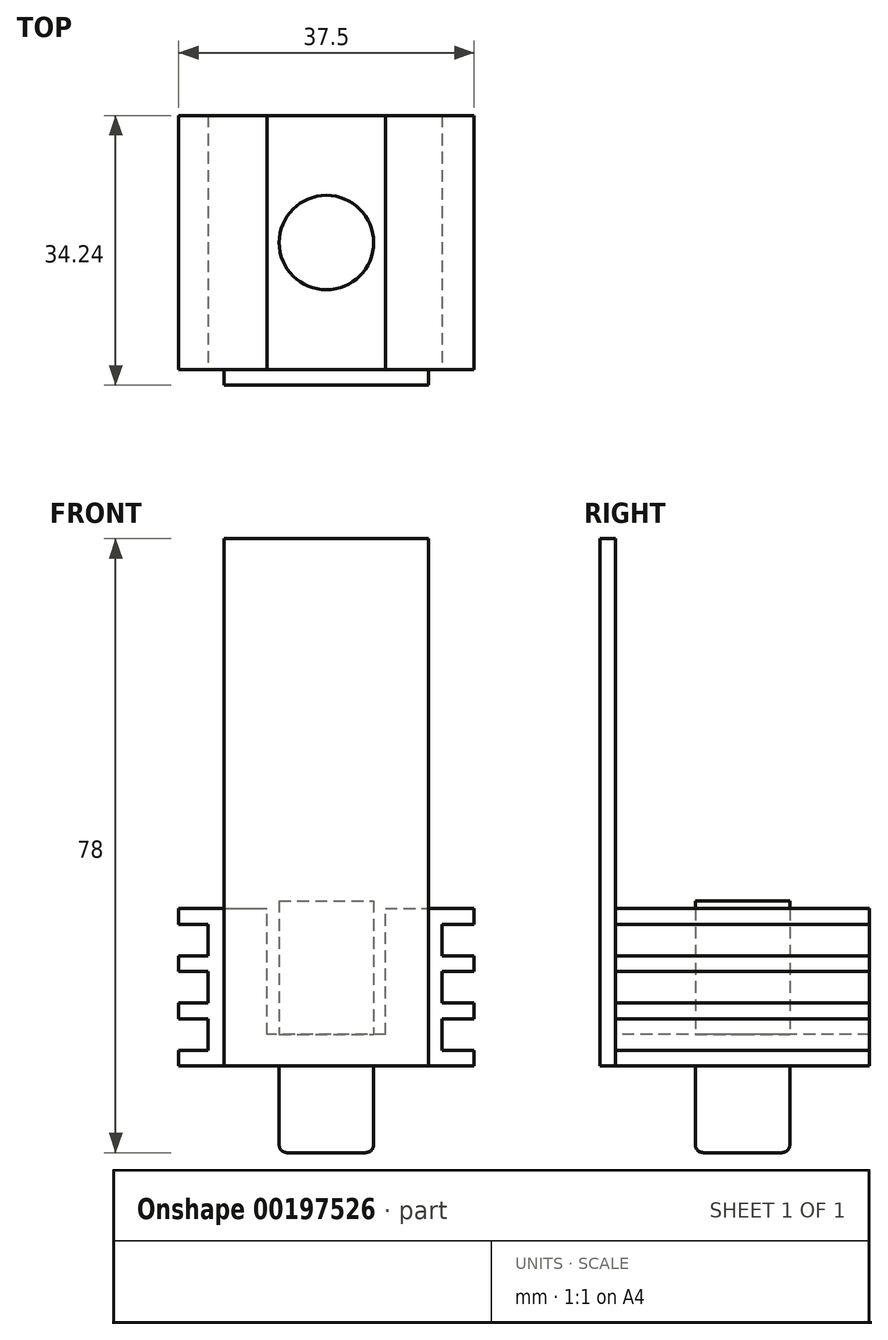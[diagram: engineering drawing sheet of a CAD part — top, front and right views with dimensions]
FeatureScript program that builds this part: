
annotation { "Feature Type Name" : "Feature", "Feature Type Description" : "" }
export const myFeature = defineFeature(function(context is Context, id is Id, definition is map)
    precondition{}
    {
        {
            var Q0;
            Q0=qCreatedBy(makeId("Top.planeOp"),FACE);
            var sketch = newSketch(context, id + "F0", { "sketchPlane" : qUnion([Q0])});
            skLineSegment(sketch, "E0.bottom", {"start": v(-18.75, 16.12) * mm, "end": v(18.75, 16.13) * mm});
            skLineSegment(sketch, "E0.top", {"start": v(-18.75, -16.13) * mm, "end": v(18.75, -16.13) * mm});
            skLineSegment(sketch, "E0.left", {"start": v(-18.75, 16.12) * mm, "end": v(-18.75, -16.13) * mm});
            skLineSegment(sketch, "E0.right", {"start": v(18.75, 16.13) * mm, "end": v(18.75, -16.12) * mm});
            skCircle(sketch, "E1", {"center": v(0, 0) * mm, "radius": 6 * mm, "construction": true});
            skSolve(sketch);
        }
        {
            var Q0;
            Q0=qSketchRegion(id+"F0",true);
            extrude(context, id + "F1", {"entities" : qUnion([Q0]), "depth" : 20 * mm});
        }
        {
            var Q0;
            Q0=makeQuery(id+"F1.opExtrude","CAP_FACE",FACE,{"disambiguationData":[OSD([sQuery(id+"F0.wireOp",EDGE,"E0.bottom"),sQuery(id+"F0.wireOp",EDGE,"E0.top"),sQuery(id+"F0.wireOp",EDGE,"E0.left"),sQuery(id+"F0.wireOp",EDGE,"E0.right")])],"isStart":true});
            var sketch = newSketch(context, id + "F2", { "sketchPlane" : qUnion([Q0])});
            skCircle(sketch, "E2.0", {"center": v(0, 0) * mm, "radius": 6 * mm});
            skSolve(sketch);
        }
        {
            var Q0;
            Q0=qSketchRegion(id+"F2",true);
            extrude(context, id + "F3", {"entities" : qUnion([Q0]), "operationType" : NewBodyOperationType.ADD, "depth" : 11 * mm});
        }
        {
            var Q0;
            Q0=makeQuery(id+"F1.opExtrude","SWEPT_FACE",FACE,{"disambiguationData":[OSD([sQuery(id+"F0.wireOp",EDGE,"E0.top")])]});
            var sketch = newSketch(context, id + "F4", { "sketchPlane" : qUnion([Q0])});
            skLineSegment(sketch, "E3.bottom", {"start": v(-7.5, 20) * mm, "end": v(7.5, 20) * mm});
            skLineSegment(sketch, "E3.top", {"start": v(-7.5, 4) * mm, "end": v(7.5, 4) * mm});
            skLineSegment(sketch, "E3.left", {"start": v(-7.5, 20) * mm, "end": v(-7.5, 4) * mm});
            skLineSegment(sketch, "E3.right", {"start": v(7.5, 20) * mm, "end": v(7.5, 4) * mm});
            skLineSegment(sketch, "E4.bottom", {"start": v(-18.75, 18) * mm, "end": v(-15.02, 18) * mm});
            skLineSegment(sketch, "E4.top", {"start": v(-18.75, 14) * mm, "end": v(-15.02, 14) * mm});
            skLineSegment(sketch, "E4.left", {"start": v(-18.75, 18) * mm, "end": v(-18.75, 14) * mm});
            skLineSegment(sketch, "E4.right", {"start": v(-15.02, 18) * mm, "end": v(-15.02, 14) * mm});
            skLineSegment(sketch, "E5.top", {"start": v(-18.75, 2) * mm, "end": v(-15.02, 2) * mm});
            skLineSegment(sketch, "E5.left", {"start": v(-18.75, 6) * mm, "end": v(-18.75, 2) * mm});
            skLineSegment(sketch, "E5.right", {"start": v(-15.02, 6) * mm, "end": v(-15.02, 2) * mm});
            skLineSegment(sketch, "E6.bottom", {"start": v(18.75, 18) * mm, "end": v(14.72, 18) * mm});
            skLineSegment(sketch, "E6.top", {"start": v(18.75, 14) * mm, "end": v(14.72, 14) * mm});
            skLineSegment(sketch, "E6.left", {"start": v(18.75, 18) * mm, "end": v(18.75, 14) * mm});
            skLineSegment(sketch, "E6.right", {"start": v(14.72, 18) * mm, "end": v(14.72, 14) * mm});
            skLineSegment(sketch, "E7.bottom", {"start": v(18.75, 8) * mm, "end": v(14.72, 8) * mm});
            skLineSegment(sketch, "E7.top", {"start": v(18.75, 12) * mm, "end": v(14.72, 12) * mm});
            skLineSegment(sketch, "E7.left", {"start": v(18.75, 8) * mm, "end": v(18.75, 12) * mm});
            skLineSegment(sketch, "E7.right", {"start": v(14.72, 8) * mm, "end": v(14.72, 12) * mm});
            skLineSegment(sketch, "E8.bottom", {"start": v(18.75, 6) * mm, "end": v(14.72, 6) * mm});
            skLineSegment(sketch, "E8.top", {"start": v(18.75, 2) * mm, "end": v(14.72, 2) * mm});
            skLineSegment(sketch, "E8.left", {"start": v(18.75, 6) * mm, "end": v(18.75, 2) * mm});
            skLineSegment(sketch, "E8.right", {"start": v(14.72, 6) * mm, "end": v(14.72, 2) * mm});
            skLineSegment(sketch, "E9", {"start": v(-15.02, 6) * mm, "end": v(-18.75, 6) * mm});
            skLineSegment(sketch, "E10.bottom", {"start": v(-18.75, 12) * mm, "end": v(-15.02, 12) * mm});
            skLineSegment(sketch, "E10.top", {"start": v(-18.75, 8) * mm, "end": v(-15.02, 8) * mm});
            skLineSegment(sketch, "E10.left", {"start": v(-18.75, 12) * mm, "end": v(-18.75, 8) * mm});
            skLineSegment(sketch, "E10.right", {"start": v(-15.02, 12) * mm, "end": v(-15.02, 8) * mm});
            skSolve(sketch);
        }
        {
            var Q0;
            Q0=qSketchRegion(id+"F4",true);
            extrude(context, id + "F5", {"entities" : qUnion([Q0]), "operationType" : NewBodyOperationType.REMOVE, "endBound" : BoundingType.THROUGH_ALL, "oppositeDirection" : true, "depth" : 25 * mm});
        }
        {
            var Q0;
            Q0=makeQuery(id+"F3.opExtrude","CAP_EDGE",EDGE,{"disambiguationData":[OSD([sQuery(id+"F2.wireOp",EDGE,"E2.0")])],"isStart":false});
            fillet(context, id + "F6", {"entities" : qUnion([Q0]), "radius" : 1 * mm, "tangentPropagation" : true, "allowEdgeOverflow" : false});
        }
        {
            var Q0;
            Q0=makeQuery(id+"F5.boolean.opBoolean","COPY",FACE,{"derivedFrom":makeQuery(id+"F5.opExtrude","SWEPT_FACE",FACE,{"disambiguationData":[OSD([sQuery(id+"F4.wireOp",EDGE,"E3.top")])]})});
            var sketch = newSketch(context, id + "F7", { "sketchPlane" : qUnion([Q0])});
            skCircle(sketch, "E11.0", {"center": v(0, 0) * mm, "radius": 6 * mm});
            skSolve(sketch);
        }
        {
            var Q0;
            Q0=qSketchRegion(id+"F7",true);
            var Q1;
            Q1=qConstructionFilter(qBodyType(qCreatedBy(id+"F7",EDGE),BodyType.WIRE),ConstructionObject.NO);
            extrude(context, id + "F8", {"entities" : qUnion([Q0]), "operationType" : NewBodyOperationType.ADD, "surfaceEntities" : qUnion([Q1]), "depth" : 17 * mm});
        }
        {
            var Q0;
            Q0=qCreatedBy(makeId("Top.planeOp"),FACE);
            var sketch = newSketch(context, id + "F9", { "sketchPlane" : qUnion([Q0])});
            skLineSegment(sketch, "E12.bottom", {"start": v(-13, -16.13) * mm, "end": v(13, -16.13) * mm});
            skLineSegment(sketch, "E12.top", {"start": v(-13, -18.13) * mm, "end": v(13, -18.13) * mm});
            skLineSegment(sketch, "E12.left", {"start": v(-13, -16.13) * mm, "end": v(-13, -18.13) * mm});
            skLineSegment(sketch, "E12.right", {"start": v(13, -16.13) * mm, "end": v(13, -18.13) * mm});
            skSolve(sketch);
        }
        {
            var Q0;
            Q0=qSketchRegion(id+"F9",true);
            extrude(context, id + "F10", {"entities" : qUnion([Q0]), "operationType" : NewBodyOperationType.ADD, "depth" : 67 * mm});
        }
    });
